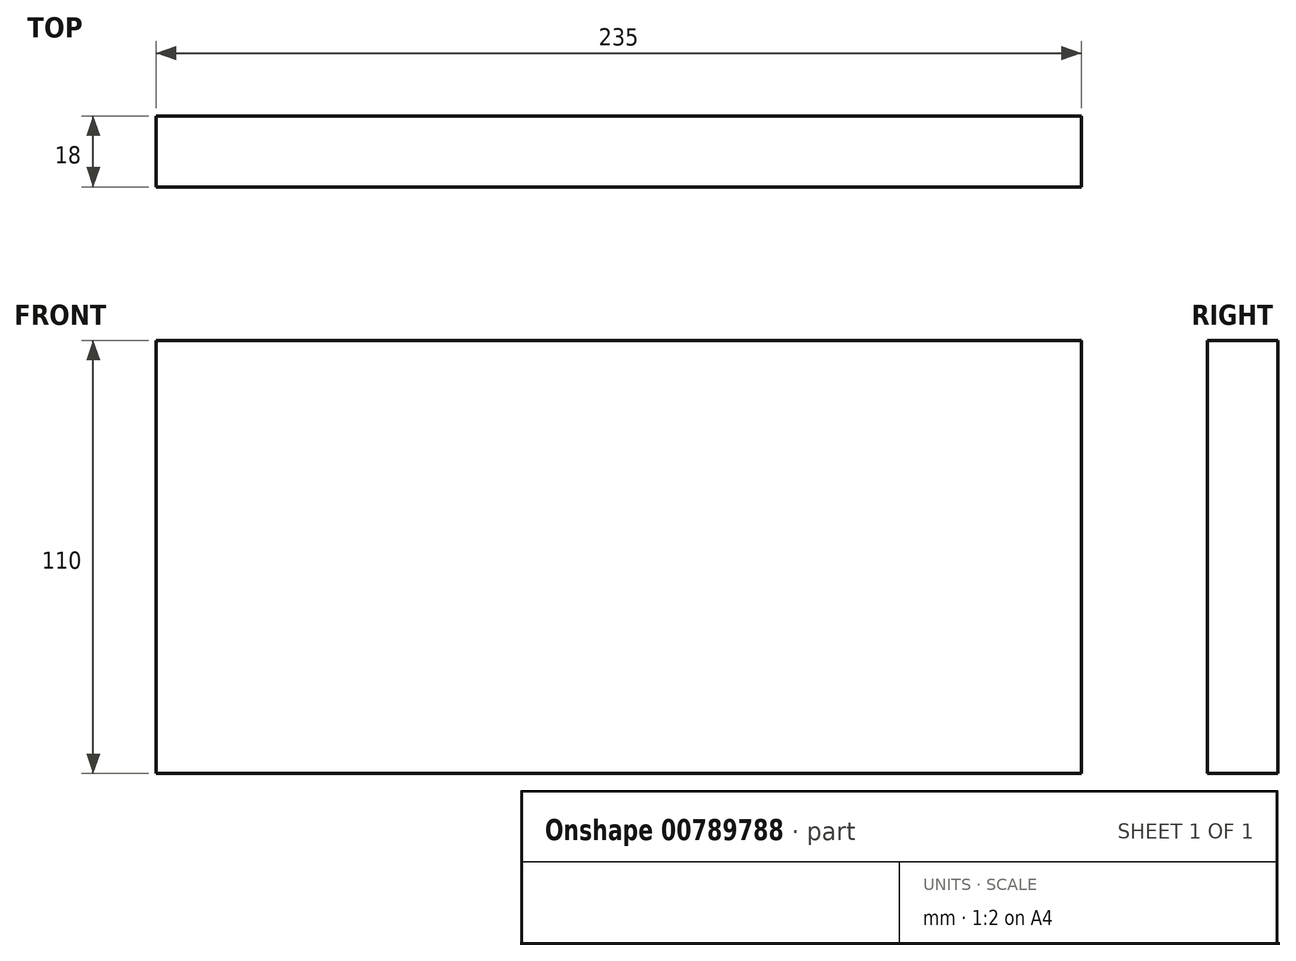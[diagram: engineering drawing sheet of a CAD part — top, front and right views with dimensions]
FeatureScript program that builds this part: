
annotation { "Feature Type Name" : "Feature", "Feature Type Description" : "" }
export const myFeature = defineFeature(function(context is Context, id is Id, definition is map)
    precondition{}
    {
        {
            var Q0;
            Q0=qCreatedBy(makeId("Front.planeOp"),FACE);
            var sketch = newSketch(context, id + "F0", { "sketchPlane" : qUnion([Q0])});
            skLineSegment(sketch, "E0.bottom", {"start": v(-115.91, 31) * mm, "end": v(119.09, 31) * mm});
            skLineSegment(sketch, "E0.top", {"start": v(-115.91, -79) * mm, "end": v(119.09, -79) * mm});
            skLineSegment(sketch, "E0.left", {"start": v(-115.91, 31) * mm, "end": v(-115.91, -79) * mm});
            skLineSegment(sketch, "E0.right", {"start": v(119.09, 31) * mm, "end": v(119.09, -79) * mm});
            skSolve(sketch);
        }
        {
            var Q0;
            Q0 = qSketchRegion(id + "F0", true);
            extrude(context, id + "F1", {"entities" : qUnion([Q0]), "depth" : 18 * mm, "offsetDistance" : 25 * mm});
        }
    });
